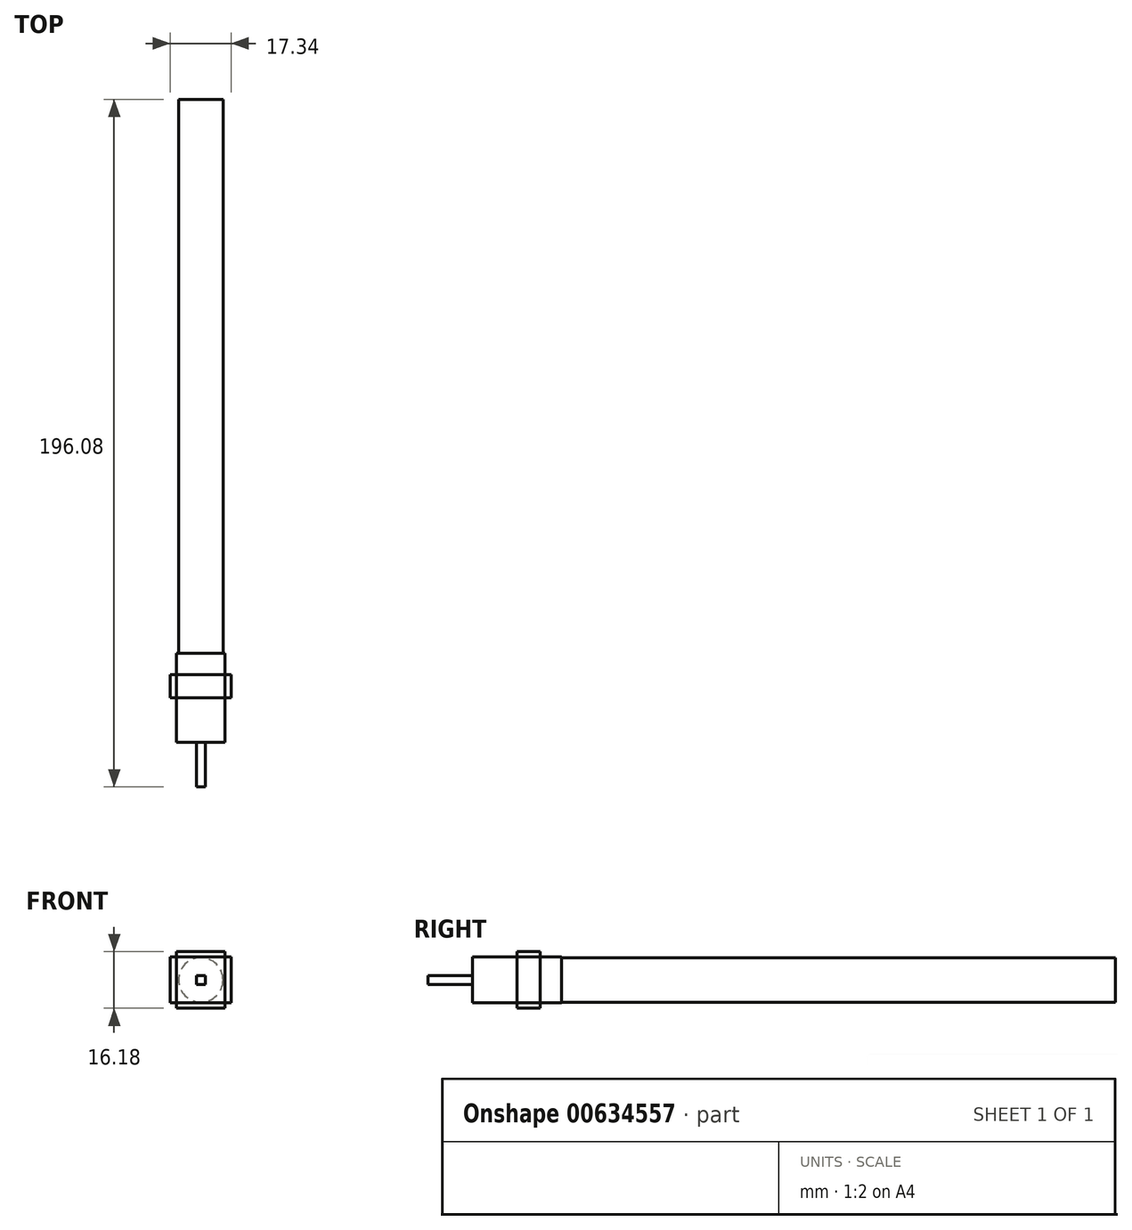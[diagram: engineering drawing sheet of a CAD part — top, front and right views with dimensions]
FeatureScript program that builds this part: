
annotation { "Feature Type Name" : "Feature", "Feature Type Description" : "" }
export const myFeature = defineFeature(function(context is Context, id is Id, definition is map)
    precondition{}
    {
        {
            var Q0;
            Q0=qCreatedBy(makeId("Front.planeOp"),FACE);
            var sketch = newSketch(context, id + "F0", { "sketchPlane" : qUnion([Q0])});
            skCircle(sketch, "E0", {"center": v(0, 0) * mm, "radius": 6.35 * mm});
            skSolve(sketch);
        }
        {
            var Q0;
            Q0 = qSketchRegion(id + "F0", true);
            extrude(context, id + "F1", {"entities" : qUnion([Q0]), "depth" : 79 * mm, "offsetDistance" : 25.4 * mm});
        }
        {
            var Q0;
            Q0=makeQuery(id+"F1.opExtrude","SWEPT_BODY",BODY,{"disambiguationData":[OSD([sQuery(id+"F0.wireOp",EDGE,"E0")])]});
            var Q1;
            Q1=qCreatedBy(makeId("Front.planeOp"),FACE);
            mirror(context, id + "F2", {"operationType" : NewBodyOperationType.ADD, "entities" : qUnion([Q0]), "mirrorPlane" : qUnion([Q1])});
        }
        {
            var Q0;
            Q0=makeQuery(id+"F1.opExtrude","CAP_FACE",FACE,{"disambiguationData":[OSD([sQuery(id+"F0.wireOp",EDGE,"E0")])],"isStart":false});
            var sketch = newSketch(context, id + "F3", { "sketchPlane" : qUnion([Q0])});
            skLineSegment(sketch, "E1.bottom", {"start": v(-6.9, 6.57) * mm, "end": v(6.9, 6.57) * mm});
            skLineSegment(sketch, "E1.top", {"start": v(-6.9, -6.57) * mm, "end": v(6.9, -6.57) * mm});
            skLineSegment(sketch, "E1.left", {"start": v(-6.9, 6.57) * mm, "end": v(-6.9, -6.57) * mm});
            skLineSegment(sketch, "E1.right", {"start": v(6.9, 6.57) * mm, "end": v(6.9, -6.57) * mm});
            skPoint(sketch, "E1.middle", {"position": v(0, 0) * mm});
            skSolve(sketch);
        }
        {
            var Q0;
            Q0 = qSketchRegion(id + "F3", true);
            extrude(context, id + "F4", {"entities" : qUnion([Q0]), "operationType" : NewBodyOperationType.ADD, "depth" : 25.4 * mm, "offsetDistance" : 25.4 * mm});
        }
        {
            var Q0;
            Q0=makeQuery(id+"F4.opExtrude","SWEPT_FACE",FACE,{"disambiguationData":[OSD([sQuery(id+"F3.wireOp",EDGE,"E1.left")])]});
            var sketch = newSketch(context, id + "F5", { "sketchPlane" : qUnion([Q0])});
            skLineSegment(sketch, "E2", {"start": v(85.06, -6.57) * mm, "end": v(85.06, 6.57) * mm});
            skLineSegment(sketch, "E3", {"start": v(91.7, -6.57) * mm, "end": v(91.7, 6.57) * mm});
            skLineSegment(sketch, "E4", {"start": v(91.7, 6.57) * mm, "end": v(85.06, 6.57) * mm});
            skLineSegment(sketch, "E5", {"start": v(85.06, -6.57) * mm, "end": v(91.7, -6.57) * mm});
            skSolve(sketch);
        }
        {
            var Q0;
            Q0 = qSketchRegion(id + "F5", true);
            extrude(context, id + "F6", {"entities" : qUnion([Q0]), "operationType" : NewBodyOperationType.ADD, "depth" : 1.78 * mm, "offsetDistance" : 25.4 * mm});
        }
        {
            var Q0;
            Q0=makeQuery(id+"F6.boolean.opBoolean","MERGE",FACE,{"derivedFrom":[makeQuery(id+"F4.opExtrude","SWEPT_FACE",FACE,{"disambiguationData":[OSD([sQuery(id+"F3.wireOp",EDGE,"E1.top")])]}),makeQuery(id+"F6.opExtrude","SWEPT_FACE",FACE,{"disambiguationData":[OSD([sQuery(id+"F5.wireOp",EDGE,"E5")])]})]});
            var sketch = newSketch(context, id + "F7", { "sketchPlane" : qUnion([Q0])});
            skLineSegment(sketch, "E6", {"start": v(-6.9, 91.7) * mm, "end": v(6.9, 91.7) * mm});
            skLineSegment(sketch, "E7", {"start": v(6.9, 91.7) * mm, "end": v(6.9, 85.06) * mm});
            skLineSegment(sketch, "E8", {"start": v(6.9, 85.06) * mm, "end": v(-6.9, 85.06) * mm});
            skLineSegment(sketch, "E9", {"start": v(-6.9, 85.06) * mm, "end": v(-6.9, 91.7) * mm});
            skSolve(sketch);
        }
        {
            var Q0;
            Q0 = qSketchRegion(id + "F7", true);
            extrude(context, id + "F8", {"entities" : qUnion([Q0]), "operationType" : NewBodyOperationType.ADD, "depth" : 1.52 * mm, "offsetDistance" : 25.4 * mm});
        }
        {
            var Q0;
            Q0=makeQuery(id+"F1.opExtrude","SWEPT_BODY",BODY,{"disambiguationData":[OSD([sQuery(id+"F0.wireOp",EDGE,"E0")])]});
            var Q1;
            Q1=qCreatedBy(makeId("Right.planeOp"),FACE);
            mirror(context, id + "F9", {"operationType" : NewBodyOperationType.ADD, "entities" : qUnion([Q0]), "mirrorPlane" : qUnion([Q1])});
        }
        {
            var Q0;
            Q0=makeQuery(id+"F1.opExtrude","SWEPT_BODY",BODY,{"disambiguationData":[OSD([sQuery(id+"F0.wireOp",EDGE,"E0")])]});
            var Q1;
            Q1=qCreatedBy(makeId("Top.planeOp"),FACE);
            mirror(context, id + "F10", {"operationType" : NewBodyOperationType.ADD, "entities" : qUnion([Q0]), "mirrorPlane" : qUnion([Q1])});
        }
        {
            var Q0;
            Q0=makeQuery(id+"F4.opExtrude","CAP_FACE",FACE,{"disambiguationData":[OSD([sQuery(id+"F3.wireOp",EDGE,"E1.bottom"),sQuery(id+"F3.wireOp",EDGE,"E1.top"),sQuery(id+"F3.wireOp",EDGE,"E1.left"),sQuery(id+"F3.wireOp",EDGE,"E1.right")])],"isStart":false});
            var sketch = newSketch(context, id + "F11", { "sketchPlane" : qUnion([Q0])});
            skLineSegment(sketch, "E10.bottom", {"start": v(-1.17, 1.27) * mm, "end": v(1.37, 1.27) * mm});
            skLineSegment(sketch, "E10.top", {"start": v(-1.17, -1.27) * mm, "end": v(1.37, -1.27) * mm});
            skLineSegment(sketch, "E10.left", {"start": v(-1.17, 1.27) * mm, "end": v(-1.17, -1.27) * mm});
            skLineSegment(sketch, "E10.right", {"start": v(1.37, 1.27) * mm, "end": v(1.37, -1.27) * mm});
            skPoint(sketch, "E10.middle", {"position": v(0.1, 0) * mm});
            skSolve(sketch);
        }
        {
            var Q0;
            Q0 = qSketchRegion(id + "F11", true);
            extrude(context, id + "F12", {"entities" : qUnion([Q0]), "operationType" : NewBodyOperationType.ADD, "depth" : 12.7 * mm, "offsetDistance" : 25.4 * mm});
        }
    });
